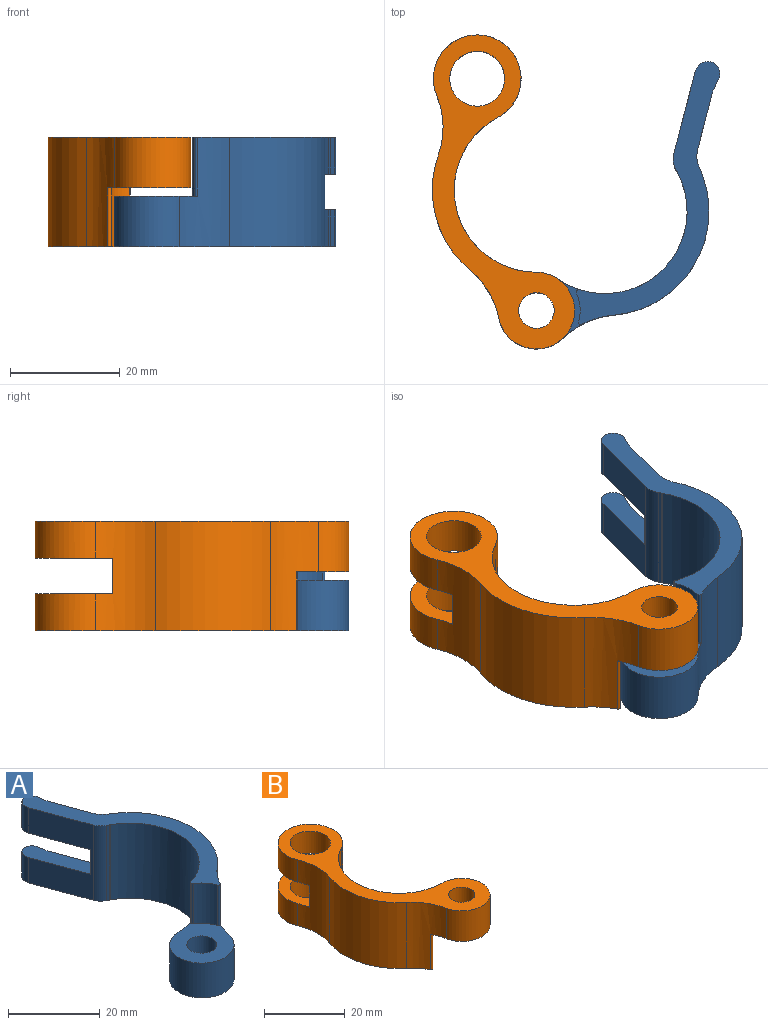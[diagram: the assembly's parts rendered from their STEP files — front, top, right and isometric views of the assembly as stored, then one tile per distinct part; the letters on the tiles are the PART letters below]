
ASSEMBLY  parts=2 mates=1
PART A: 32 faces, bbox 26x62.6x20 mm
  f0: plane 10.08x6.75mm, normal (0.94,0.34,0), area 72.4mm2, adj f4,f22,f24,f31
  f1: plane 6.75x1.82mm, normal (0.99,0.15,0), area 12.4mm2, adj f4,f22,f27,f31
  f2: cylinder r=8mm len=20mm, axis (0,0,-1), area 3.3mm2, adj f3,f4,f6,f19
  f3: plane 53.16x20.09mm, normal (0,0,1), area 244.6mm2, adj f2,f6,f8,f9,f10,f11,f13,f14
  f4: plane 62.56x26mm, normal (0,0,-1), area 374.8mm2, adj f0,f1,f2,f5,f6,f7,f8,f9
  f5: cylinder r=7mm len=14mm, axis (0,0,-1), area 292.5mm2, adj f4,f6,f8,f12
  f6: cylinder r=15mm len=28.24mm, axis (0,0,-1), area 749.2mm2, adj f2,f3,f4,f5,f12,f13
  f7: cylinder r=3.25mm len=9.25mm, axis (0,0,-1), area 188.9mm2, adj f4,f12
  f8: cylinder r=15mm len=20mm, axis (0,0,1), area 160.9mm2, adj f3,f4,f5,f9,f12,f14
  f9: cylinder r=19mm len=31.06mm, axis (0,0,-1), area 729.5mm2, adj f3,f4,f8,f20,f21,f22,f23,f24
  f10: cylinder r=8mm len=10.75mm, axis (0,0,-1), area 58.5mm2, adj f3,f12,f14,f15
  f11: plane 10.75x0.1mm, normal (-1,0,0), area 1.1mm2, adj f3,f12,f13,f15
  f12: plane 15.26x14.62mm, normal (0,0,1), area 130.2mm2, adj f5,f6,f7,f8,f10,f11,f13,f14
  f13: cylinder r=0.39mm len=10.75mm, axis (0,0,-1), area 5.4mm2, adj f3,f6,f11,f12
  f14: cylinder r=0.39mm len=10.75mm, axis (0,0,1), area 9.7mm2, adj f3,f8,f10,f12
  f15: cylinder r=0.39mm len=10.75mm, axis (0,0,-1), area 4.3mm2, adj f3,f10,f11,f12
  f16: plane 20x14.5mm, normal (-0.94,-0.34,0), area 211.9mm2, adj f3,f4,f20,f21,f22,f25,f28,f29
  f17: plane 10.08x6.75mm, normal (0.94,0.34,0), area 72.4mm2, adj f3,f21,f23,f30
  f18: plane 6.75x1.82mm, normal (0.99,0.15,0), area 12.4mm2, adj f3,f21,f26,f30
  f19: cylinder r=14.57mm len=20mm, axis (0,0,1), area 11.8mm2, adj f2,f3,f4,f25
  f20: plane 6.5x5.57mm, normal (0,1,0), area 36.2mm2, adj f9,f16,f21,f22
  f21: plane 17.26x10.86mm, normal (0,0,-1), area 73mm2, adj f9,f16,f17,f18,f20,f23,f26,f28
  f22: plane 17.26x10.86mm, normal (0,0,1), area 73mm2, adj f0,f1,f9,f16,f20,f24,f27,f29
  f23: cylinder r=5mm len=6.75mm, axis (0,0,-1), area 23.2mm2, adj f3,f9,f17,f21
  f24: cylinder r=5mm len=6.75mm, axis (0,0,-1), area 23.2mm2, adj f0,f4,f9,f22
  f25: cylinder r=4mm len=20mm, axis (0,0,1), area 61.4mm2, adj f3,f4,f16,f19
  f26: cylinder r=2.25mm len=6.75mm, axis (0,0,1), area 26.9mm2, adj f3,f18,f21,f28
  f27: cylinder r=2.25mm len=6.75mm, axis (0,0,1), area 26.9mm2, adj f1,f4,f22,f29
  f28: cylinder r=2.5mm len=6.75mm, axis (0,0,1), area 24.8mm2, adj f3,f16,f21,f26
  f29: cylinder r=2.5mm len=6.75mm, axis (0,0,1), area 24.8mm2, adj f4,f16,f22,f27
  f30: cylinder r=4mm len=6.75mm, axis (0,0,-1), area 5.4mm2, adj f3,f17,f18,f21
  f31: cylinder r=4mm len=6.75mm, axis (0,0,-1), area 5.4mm2, adj f0,f1,f4,f22
PART B: 20 faces, bbox 26x57.3x20 mm
  f0: cylinder r=5mm len=10mm, axis (0,0,-1), area 212.1mm2, adj f2,f18
  f1: cylinder r=15mm len=28.24mm, axis (0,0,-1), area 749.2mm2, adj f2,f4,f5,f8,f13,f14
  f2: plane 47.9x16.2mm, normal (0,0,-1), area 279.7mm2, adj f0,f1,f3,f5,f9,f10,f11,f12
  f3: cylinder r=19mm len=21.07mm, axis (0,0,-1), area 466mm2, adj f2,f8,f9,f10
  f4: cylinder r=7mm len=14mm, axis (0,0,-1), area 292.5mm2, adj f1,f8,f9,f13
  f5: cylinder r=8mm len=20mm, axis (0,0,-1), area 509mm2, adj f1,f2,f8,f10,f17,f18,f19
  f6: cylinder r=3.25mm len=9.25mm, axis (0,0,-1), area 188.9mm2, adj f8,f13
  f7: cylinder r=5mm len=10mm, axis (0,0,-1), area 212.1mm2, adj f8,f17
  f8: plane 57.31x26mm, normal (0,0,1), area 409.9mm2, adj f1,f3,f4,f5,f6,f7,f9,f10
  f9: cylinder r=15mm len=20mm, axis (0,0,1), area 160.9mm2, adj f2,f3,f4,f8,f13,f15
  f10: cylinder r=15mm len=20mm, axis (0,0,1), area 200.5mm2, adj f2,f3,f5,f8,f17,f18,f19
  f11: cylinder r=8mm len=10.75mm, axis (0,0,1), area 58.5mm2, adj f2,f13,f15,f16
  f12: plane 10.75x0.1mm, normal (1,0,0), area 1.1mm2, adj f2,f13,f14,f16
  f13: plane 15.26x14.62mm, normal (0,0,-1), area 130.2mm2, adj f1,f4,f6,f9,f11,f12,f14,f15
  f14: cylinder r=0.39mm len=10.75mm, axis (0,0,-1), area 5.4mm2, adj f1,f2,f12,f13
  f15: cylinder r=0.39mm len=10.75mm, axis (0,0,1), area 9.7mm2, adj f2,f9,f11,f13
  f16: cylinder r=0.39mm len=10.75mm, axis (0,0,1), area 4.3mm2, adj f2,f11,f12,f13
  f17: plane 16x14.21mm, normal (0,0,-1), area 111.5mm2, adj f5,f7,f10,f19
  f18: plane 16x14.21mm, normal (0,0,1), area 111.5mm2, adj f0,f5,f10,f19
  f19: plane 11.51x6.5mm, normal (0,1,0), area 74.8mm2, adj f5,f10,f17,f18
PLACE A rot(axis=(0,0,-1),34.7deg) t=(12.51,-3.9,0)mm
PLACE B at identity fixed
MATE revolute B.f11 <-> A.f5  axis (0,0,-1) through (0,-22,0.75)mm
